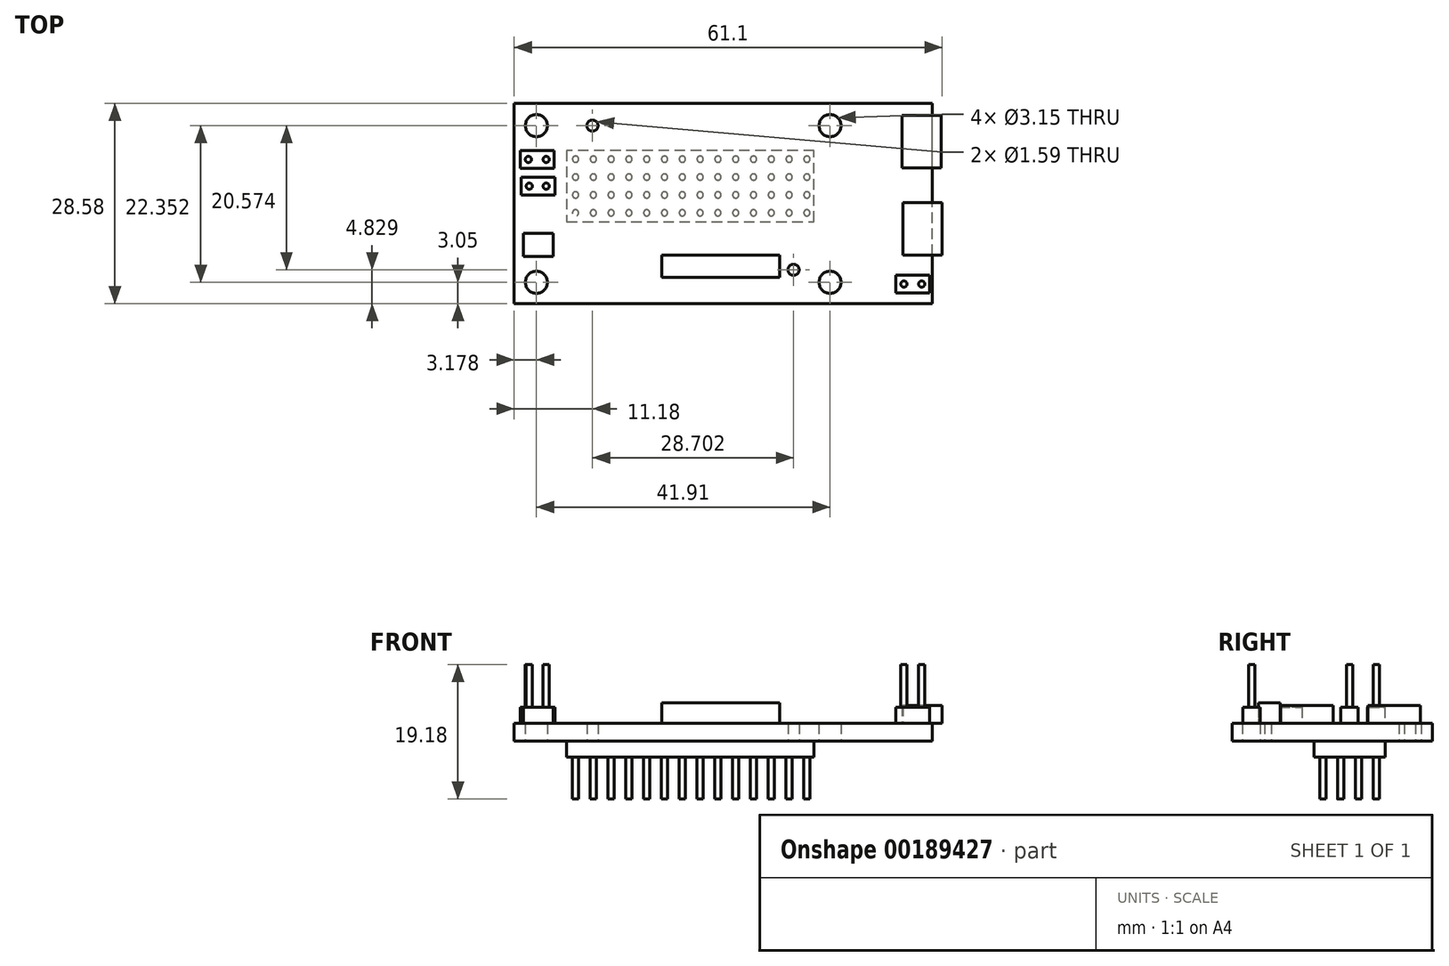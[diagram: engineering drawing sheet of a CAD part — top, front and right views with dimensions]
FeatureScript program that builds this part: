
annotation { "Feature Type Name" : "Feature", "Feature Type Description" : "" }
export const myFeature = defineFeature(function(context is Context, id is Id, definition is map)
    precondition{}
    {
        {
            var Q0;
            Q0=qCreatedBy(makeId("Top.planeOp"),FACE);
            var sketch = newSketch(context, id + "F0", { "sketchPlane" : qUnion([Q0])});
            skLineSegment(sketch, "E0", {"start": v(-22.44, -2) * mm, "end": v(-22.44, -0.67) * mm});
            skLineSegment(sketch, "E1", {"start": v(-22.44, -0.67) * mm, "end": v(-21.12, -0.67) * mm});
            skLineSegment(sketch, "E2", {"start": v(-21.12, -0.67) * mm, "end": v(-21.12, -2) * mm});
            skLineSegment(sketch, "E3", {"start": v(-21.12, -2) * mm, "end": v(-22.44, -2) * mm});
            skLineSegment(sketch, "E4", {"start": v(-22.44, 0.55) * mm, "end": v(-22.44, 1.87) * mm});
            skLineSegment(sketch, "E5", {"start": v(-22.44, 1.87) * mm, "end": v(-21.12, 1.87) * mm});
            skLineSegment(sketch, "E6", {"start": v(-21.12, 1.87) * mm, "end": v(-21.12, 0.55) * mm});
            skLineSegment(sketch, "E7", {"start": v(-21.12, 0.55) * mm, "end": v(-22.44, 0.55) * mm});
            skLineSegment(sketch, "E8", {"start": v(-22.44, 3.09) * mm, "end": v(-22.44, 4.4) * mm});
            skLineSegment(sketch, "E9", {"start": v(-22.44, 4.4) * mm, "end": v(-21.12, 4.4) * mm});
            skLineSegment(sketch, "E10", {"start": v(-21.12, 4.4) * mm, "end": v(-21.12, 3.09) * mm});
            skLineSegment(sketch, "E11", {"start": v(-21.12, 3.09) * mm, "end": v(-22.44, 3.09) * mm});
            skLineSegment(sketch, "E12", {"start": v(-22.44, 5.63) * mm, "end": v(-22.44, 6.95) * mm});
            skLineSegment(sketch, "E13", {"start": v(-22.44, 6.95) * mm, "end": v(-21.12, 6.95) * mm});
            skLineSegment(sketch, "E14", {"start": v(-21.12, 6.95) * mm, "end": v(-21.12, 5.63) * mm});
            skLineSegment(sketch, "E15", {"start": v(-21.12, 5.63) * mm, "end": v(-22.44, 5.63) * mm});
            skLineSegment(sketch, "E16", {"start": v(26.9, -10.78) * mm, "end": v(28.33, -10.78) * mm});
            skLineSegment(sketch, "E17", {"start": v(28.33, -10.78) * mm, "end": v(28.33, -12.2) * mm});
            skLineSegment(sketch, "E18", {"start": v(28.33, -12.2) * mm, "end": v(26.9, -12.2) * mm});
            skLineSegment(sketch, "E19", {"start": v(26.9, -12.2) * mm, "end": v(26.9, -10.78) * mm});
            skLineSegment(sketch, "E20", {"start": v(-27.68, 1.77) * mm, "end": v(-29.1, 1.77) * mm});
            skLineSegment(sketch, "E21", {"start": v(-29.1, 1.77) * mm, "end": v(-29.1, 3.19) * mm});
            skLineSegment(sketch, "E22", {"start": v(-29.1, 3.19) * mm, "end": v(-27.68, 3.19) * mm});
            skLineSegment(sketch, "E23", {"start": v(-27.68, 3.19) * mm, "end": v(-27.68, 1.77) * mm});
            skLineSegment(sketch, "E24", {"start": v(-27.8, 5.58) * mm, "end": v(-29.23, 5.58) * mm});
            skLineSegment(sketch, "E25", {"start": v(-29.23, 5.58) * mm, "end": v(-29.23, 7) * mm});
            skLineSegment(sketch, "E26", {"start": v(-29.23, 7) * mm, "end": v(-27.8, 7) * mm});
            skLineSegment(sketch, "E27", {"start": v(-27.8, 7) * mm, "end": v(-27.8, 5.58) * mm});
            skLineSegment(sketch, "E28", {"start": v(24.95, -7.37) * mm, "end": v(30.55, -7.37) * mm});
            skLineSegment(sketch, "E29", {"start": v(30.55, -7.37) * mm, "end": v(30.55, 0.13) * mm});
            skLineSegment(sketch, "E30", {"start": v(30.55, 0.13) * mm, "end": v(24.95, 0.13) * mm});
            skLineSegment(sketch, "E31", {"start": v(24.95, 0.13) * mm, "end": v(24.95, -7.37) * mm});
            skLineSegment(sketch, "E32", {"start": v(-29.24, -4.28) * mm, "end": v(-25, -4.28) * mm});
            skLineSegment(sketch, "E33", {"start": v(-25, -4.28) * mm, "end": v(-25, -7.53) * mm});
            skLineSegment(sketch, "E34", {"start": v(-25, -7.53) * mm, "end": v(-29.24, -7.53) * mm});
            skLineSegment(sketch, "E35", {"start": v(-29.24, -7.53) * mm, "end": v(-29.24, -4.28) * mm});
            skLineSegment(sketch, "E36", {"start": v(-23.05, -0.06) * mm, "end": v(-23.05, -2.6) * mm});
            skLineSegment(sketch, "E37", {"start": v(-23.05, -2.6) * mm, "end": v(2.35, -2.6) * mm});
            skLineSegment(sketch, "E38", {"start": v(2.35, -0.06) * mm, "end": v(-23.05, -0.06) * mm});
            skLineSegment(sketch, "E39", {"start": v(-23.05, 2.48) * mm, "end": v(-23.05, -0.06) * mm});
            skLineSegment(sketch, "E40", {"start": v(-23.05, -0.06) * mm, "end": v(2.35, -0.06) * mm});
            skLineSegment(sketch, "E41", {"start": v(2.35, 2.48) * mm, "end": v(-23.05, 2.48) * mm});
            skLineSegment(sketch, "E42", {"start": v(-23.05, 5.02) * mm, "end": v(-23.05, 2.48) * mm});
            skLineSegment(sketch, "E43", {"start": v(-23.05, 2.48) * mm, "end": v(2.35, 2.48) * mm});
            skLineSegment(sketch, "E44", {"start": v(2.35, 5.02) * mm, "end": v(-23.05, 5.02) * mm});
            skLineSegment(sketch, "E45", {"start": v(-23.05, 7.56) * mm, "end": v(-23.05, 5.02) * mm});
            skLineSegment(sketch, "E46", {"start": v(-23.05, 5.02) * mm, "end": v(2.35, 5.02) * mm});
            skLineSegment(sketch, "E47", {"start": v(2.35, 7.56) * mm, "end": v(-23.05, 7.56) * mm});
            skLineSegment(sketch, "E48", {"start": v(-9.46, -7.4) * mm, "end": v(7.34, -7.4) * mm});
            skLineSegment(sketch, "E49", {"start": v(7.34, -7.4) * mm, "end": v(7.34, -10.53) * mm});
            skLineSegment(sketch, "E50", {"start": v(7.34, -10.53) * mm, "end": v(-9.46, -10.53) * mm});
            skLineSegment(sketch, "E51", {"start": v(-9.46, -10.53) * mm, "end": v(-9.46, -7.4) * mm});
            skLineSegment(sketch, "E52", {"start": v(24.82, 5.08) * mm, "end": v(30.42, 5.08) * mm});
            skLineSegment(sketch, "E53", {"start": v(30.42, 5.08) * mm, "end": v(30.42, 12.58) * mm});
            skLineSegment(sketch, "E54", {"start": v(30.42, 12.58) * mm, "end": v(24.82, 12.58) * mm});
            skLineSegment(sketch, "E55", {"start": v(24.82, 12.58) * mm, "end": v(24.82, 5.08) * mm});
            skLineSegment(sketch, "E56", {"start": v(28.76, -10.25) * mm, "end": v(28.76, -12.74) * mm});
            skLineSegment(sketch, "E57", {"start": v(28.76, -12.74) * mm, "end": v(23.94, -12.74) * mm});
            skLineSegment(sketch, "E58", {"start": v(23.94, -12.74) * mm, "end": v(23.94, -10.25) * mm});
            skLineSegment(sketch, "E59", {"start": v(23.94, -10.25) * mm, "end": v(28.76, -10.25) * mm});
            skLineSegment(sketch, "E60", {"start": v(-29.53, 1.23) * mm, "end": v(-29.53, 3.72) * mm});
            skLineSegment(sketch, "E61", {"start": v(-29.53, 3.72) * mm, "end": v(-24.7, 3.72) * mm});
            skLineSegment(sketch, "E62", {"start": v(-24.7, 3.72) * mm, "end": v(-24.7, 1.23) * mm});
            skLineSegment(sketch, "E63", {"start": v(-24.7, 1.23) * mm, "end": v(-29.53, 1.23) * mm});
            skLineSegment(sketch, "E64", {"start": v(-29.66, 5.04) * mm, "end": v(-29.66, 7.53) * mm});
            skLineSegment(sketch, "E65", {"start": v(-29.66, 7.53) * mm, "end": v(-24.83, 7.53) * mm});
            skLineSegment(sketch, "E66", {"start": v(-24.83, 7.53) * mm, "end": v(-24.83, 5.04) * mm});
            skLineSegment(sketch, "E67", {"start": v(-24.83, 5.04) * mm, "end": v(-29.66, 5.04) * mm});
            skLineSegment(sketch, "E68", {"start": v(12.25, 5.02) * mm, "end": v(-13.15, 5.02) * mm});
            skLineSegment(sketch, "E69", {"start": v(-13.15, 5.02) * mm, "end": v(12.25, 5.02) * mm});
            skLineSegment(sketch, "E70", {"start": v(12.25, 5.02) * mm, "end": v(12.25, 7.56) * mm});
            skLineSegment(sketch, "E71", {"start": v(12.25, 7.56) * mm, "end": v(-13.15, 7.56) * mm});
            skLineSegment(sketch, "E72", {"start": v(12.25, -0.06) * mm, "end": v(-13.15, -0.06) * mm});
            skLineSegment(sketch, "E73", {"start": v(-13.15, -0.06) * mm, "end": v(12.25, -0.06) * mm});
            skLineSegment(sketch, "E74", {"start": v(12.25, -0.06) * mm, "end": v(12.25, 2.48) * mm});
            skLineSegment(sketch, "E75", {"start": v(12.25, 2.48) * mm, "end": v(-13.15, 2.48) * mm});
            skLineSegment(sketch, "E76", {"start": v(-13.15, 2.48) * mm, "end": v(12.25, 2.48) * mm});
            skLineSegment(sketch, "E77", {"start": v(12.25, 2.48) * mm, "end": v(12.25, 5.02) * mm});
            skLineSegment(sketch, "E78", {"start": v(-13.15, -2.6) * mm, "end": v(12.25, -2.6) * mm});
            skLineSegment(sketch, "E79", {"start": v(12.25, -2.6) * mm, "end": v(12.25, -0.06) * mm});
            skLineSegment(sketch, "E80", {"start": v(-30.55, 14.29) * mm, "end": v(-30.55, -14.29) * mm});
            skLineSegment(sketch, "E81", {"start": v(-30.55, -14.29) * mm, "end": v(29.14, -14.29) * mm});
            skLineSegment(sketch, "E82", {"start": v(29.14, -14.29) * mm, "end": v(29.14, 14.29) * mm});
            skLineSegment(sketch, "E83", {"start": v(29.14, 14.29) * mm, "end": v(-30.55, 14.29) * mm});
            skSolve(sketch);
        }
        {
            var Q0;
            Q0=qCreatedBy(makeId("Top.planeOp"),FACE);
            var sketch = newSketch(context, id + "F1", { "sketchPlane" : qUnion([Q0])});
            skLineSegment(sketch, "E84.0", {"start": v(-30.55, 14.29) * mm, "end": v(-30.55, -14.29) * mm});
            skLineSegment(sketch, "E84.1", {"start": v(-30.55, -14.29) * mm, "end": v(29.14, -14.29) * mm});
            skLineSegment(sketch, "E84.2", {"start": v(29.14, 14.29) * mm, "end": v(-30.55, 14.29) * mm});
            skLineSegment(sketch, "E84.3", {"start": v(29.14, -14.29) * mm, "end": v(29.14, 14.29) * mm});
            skCircle(sketch, "E85", {"center": v(-27.37, 11.11) * mm, "radius": 1.57 * mm});
            skCircle(sketch, "E86", {"center": v(14.54, 11.11) * mm, "radius": 1.57 * mm});
            skCircle(sketch, "E87", {"center": v(14.54, -11.24) * mm, "radius": 1.57 * mm});
            skCircle(sketch, "E88", {"center": v(-27.37, -11.24) * mm, "radius": 1.57 * mm});
            skCircle(sketch, "E89", {"center": v(-19.37, 11.11) * mm, "radius": 0.8 * mm});
            skCircle(sketch, "E90", {"center": v(9.33, -9.46) * mm, "radius": 0.8 * mm});
            skSolve(sketch);
        }
        {
            var Q0;
            Q0 = qSketchRegion(id + "F1", true);
            extrude(context, id + "F2", {"entities" : qUnion([Q0]), "depth" : 2.54 * mm});
        }
        {
            var Q0;
            Q0=makeQuery(id+"F2.opExtrude","CAP_FACE",FACE,{"disambiguationData":[OSD([sQuery(id+"F1.wireOp",EDGE,"E84.0"),sQuery(id+"F1.wireOp",EDGE,"E84.1"),sQuery(id+"F1.wireOp",EDGE,"E84.2"),sQuery(id+"F1.wireOp",EDGE,"E84.3"),sQuery(id+"F1.wireOp",EDGE,"E85"),sQuery(id+"F1.wireOp",EDGE,"E86"),sQuery(id+"F1.wireOp",EDGE,"E87"),sQuery(id+"F1.wireOp",EDGE,"E88"),sQuery(id+"F1.wireOp",EDGE,"E89"),sQuery(id+"F1.wireOp",EDGE,"E90")])],"isStart":false});
            var sketch = newSketch(context, id + "F3", { "sketchPlane" : qUnion([Q0])});
            skLineSegment(sketch, "E91.0", {"start": v(30.42, 12.58) * mm, "end": v(24.82, 12.58) * mm});
            skLineSegment(sketch, "E91.1", {"start": v(30.42, 5.08) * mm, "end": v(30.42, 12.58) * mm});
            skLineSegment(sketch, "E91.2", {"start": v(24.82, 5.08) * mm, "end": v(30.42, 5.08) * mm});
            skLineSegment(sketch, "E91.3", {"start": v(24.82, 12.58) * mm, "end": v(24.82, 5.08) * mm});
            skLineSegment(sketch, "E91.4", {"start": v(30.55, 0.13) * mm, "end": v(24.95, 0.13) * mm});
            skLineSegment(sketch, "E91.5", {"start": v(30.55, -7.37) * mm, "end": v(30.55, 0.13) * mm});
            skLineSegment(sketch, "E91.6", {"start": v(24.95, -7.37) * mm, "end": v(30.55, -7.37) * mm});
            skLineSegment(sketch, "E91.7", {"start": v(24.95, 0.13) * mm, "end": v(24.95, -7.37) * mm});
            skSolve(sketch);
        }
        {
            var Q0;
            Q0 = qSketchRegion(id + "F3", true);
            extrude(context, id + "F4", {"entities" : qUnion([Q0]), "operationType" : NewBodyOperationType.ADD, "depth" : 2.54 * mm});
        }
        {
            var Q0;
            Q0=makeQuery(id+"F2.opExtrude","CAP_FACE",FACE,{"disambiguationData":[OSD([sQuery(id+"F1.wireOp",EDGE,"E84.0"),sQuery(id+"F1.wireOp",EDGE,"E84.1"),sQuery(id+"F1.wireOp",EDGE,"E84.2"),sQuery(id+"F1.wireOp",EDGE,"E84.3"),sQuery(id+"F1.wireOp",EDGE,"E85"),sQuery(id+"F1.wireOp",EDGE,"E86"),sQuery(id+"F1.wireOp",EDGE,"E87"),sQuery(id+"F1.wireOp",EDGE,"E88"),sQuery(id+"F1.wireOp",EDGE,"E89"),sQuery(id+"F1.wireOp",EDGE,"E90")])],"isStart":false});
            var sketch = newSketch(context, id + "F5", { "sketchPlane" : qUnion([Q0])});
            skLineSegment(sketch, "E92.0", {"start": v(-9.46, -7.4) * mm, "end": v(7.34, -7.4) * mm});
            skLineSegment(sketch, "E92.1", {"start": v(7.34, -7.4) * mm, "end": v(7.34, -10.53) * mm});
            skLineSegment(sketch, "E92.2", {"start": v(7.34, -10.53) * mm, "end": v(-9.46, -10.53) * mm});
            skLineSegment(sketch, "E92.3", {"start": v(-9.46, -10.53) * mm, "end": v(-9.46, -7.4) * mm});
            skSolve(sketch);
        }
        {
            var Q0;
            Q0 = qSketchRegion(id + "F5", true);
            extrude(context, id + "F6", {"entities" : qUnion([Q0]), "operationType" : NewBodyOperationType.ADD, "depth" : 2.92 * mm});
        }
        {
            var Q0;
            Q0=makeQuery(id+"F2.opExtrude","CAP_FACE",FACE,{"disambiguationData":[OSD([sQuery(id+"F1.wireOp",EDGE,"E84.0"),sQuery(id+"F1.wireOp",EDGE,"E84.1"),sQuery(id+"F1.wireOp",EDGE,"E84.2"),sQuery(id+"F1.wireOp",EDGE,"E84.3"),sQuery(id+"F1.wireOp",EDGE,"E85"),sQuery(id+"F1.wireOp",EDGE,"E86"),sQuery(id+"F1.wireOp",EDGE,"E87"),sQuery(id+"F1.wireOp",EDGE,"E88"),sQuery(id+"F1.wireOp",EDGE,"E89"),sQuery(id+"F1.wireOp",EDGE,"E90")])],"isStart":false});
            var sketch = newSketch(context, id + "F7", { "sketchPlane" : qUnion([Q0])});
            skLineSegment(sketch, "E93.0", {"start": v(23.94, -10.25) * mm, "end": v(28.76, -10.25) * mm});
            skLineSegment(sketch, "E93.1", {"start": v(23.94, -12.74) * mm, "end": v(23.94, -10.25) * mm});
            skLineSegment(sketch, "E93.2", {"start": v(28.76, -12.74) * mm, "end": v(23.94, -12.74) * mm});
            skLineSegment(sketch, "E93.3", {"start": v(28.76, -10.25) * mm, "end": v(28.76, -12.74) * mm});
            skLineSegment(sketch, "E93.4", {"start": v(-24.83, 5.04) * mm, "end": v(-29.66, 5.04) * mm});
            skLineSegment(sketch, "E93.5", {"start": v(-24.83, 7.53) * mm, "end": v(-24.83, 5.04) * mm});
            skLineSegment(sketch, "E93.6", {"start": v(-29.66, 7.53) * mm, "end": v(-24.83, 7.53) * mm});
            skLineSegment(sketch, "E93.7", {"start": v(-29.66, 5.04) * mm, "end": v(-29.66, 7.53) * mm});
            skLineSegment(sketch, "E93.8", {"start": v(-29.53, 1.23) * mm, "end": v(-29.53, 3.72) * mm});
            skLineSegment(sketch, "E93.9", {"start": v(-29.53, 3.72) * mm, "end": v(-24.7, 3.72) * mm});
            skLineSegment(sketch, "E93.10", {"start": v(-24.7, 3.72) * mm, "end": v(-24.7, 1.23) * mm});
            skLineSegment(sketch, "E93.11", {"start": v(-24.7, 1.23) * mm, "end": v(-29.53, 1.23) * mm});
            skLineSegment(sketch, "E93.12", {"start": v(-29.24, -4.28) * mm, "end": v(-25, -4.28) * mm});
            skLineSegment(sketch, "E93.13", {"start": v(-25, -4.28) * mm, "end": v(-25, -7.53) * mm});
            skLineSegment(sketch, "E93.14", {"start": v(-25, -7.53) * mm, "end": v(-29.24, -7.53) * mm});
            skLineSegment(sketch, "E93.15", {"start": v(-29.24, -7.53) * mm, "end": v(-29.24, -4.28) * mm});
            skSolve(sketch);
        }
        {
            var Q0;
            Q0 = qSketchRegion(id + "F7", true);
            extrude(context, id + "F8", {"entities" : qUnion([Q0]), "operationType" : NewBodyOperationType.ADD, "depth" : 2.3 * mm});
        }
        {
            var Q0;
            Q0=makeQuery(id+"F8.opExtrude","CAP_FACE",FACE,{"disambiguationData":[OSD([sQuery(id+"F7.wireOp",EDGE,"E93.4"),sQuery(id+"F7.wireOp",EDGE,"E93.5"),sQuery(id+"F7.wireOp",EDGE,"E93.6"),sQuery(id+"F7.wireOp",EDGE,"E93.7")])],"isStart":false});
            var sketch = newSketch(context, id + "F9", { "sketchPlane" : qUnion([Q0])});
            skCircle(sketch, "E94", {"center": v(-28.51, 6.29) * mm, "radius": 0.44 * mm});
            skCircle(sketch, "E95", {"center": v(-25.97, 6.29) * mm, "radius": 0.44 * mm});
            skCircle(sketch, "E96", {"center": v(-28.39, 2.48) * mm, "radius": 0.44 * mm});
            skCircle(sketch, "E97", {"center": v(-25.97, 2.48) * mm, "radius": 0.44 * mm});
            skCircle(sketch, "E98", {"center": v(27.62, -11.5) * mm, "radius": 0.44 * mm});
            skCircle(sketch, "E99", {"center": v(25.08, -11.5) * mm, "radius": 0.44 * mm});
            skPoint(sketch, "E100.0", {"position": v(28.33, -10.78) * mm});
            skPoint(sketch, "E100.1", {"position": v(26.9, -12.2) * mm});
            skLineSegment(sketch, "E101", {"start": v(28.33, -10.78) * mm, "end": v(26.9, -12.2) * mm, "construction": true});
            skPoint(sketch, "E102.0", {"position": v(-27.8, 7) * mm});
            skPoint(sketch, "E102.1", {"position": v(-29.23, 5.58) * mm});
            skPoint(sketch, "E102.2", {"position": v(-29.1, 3.19) * mm});
            skPoint(sketch, "E102.3", {"position": v(-27.68, 1.77) * mm});
            skLineSegment(sketch, "E103", {"start": v(-27.8, 7) * mm, "end": v(-29.23, 5.58) * mm, "construction": true});
            skLineSegment(sketch, "E104", {"start": v(-29.1, 3.19) * mm, "end": v(-27.68, 1.77) * mm, "construction": true});
            skSolve(sketch);
        }
        {
            var Q0;
            Q0 = qSketchRegion(id + "F9", true);
            extrude(context, id + "F10", {"entities" : qUnion([Q0]), "operationType" : NewBodyOperationType.ADD, "depth" : 6.1 * mm});
        }
        {
            var Q0;
            {var subQ9=sQuery(id+"F0.wireOp",EDGE,"E31");Q0=makeQuery(id+"F0.imprint","IMPRINT",FACE,{"disambiguationData":[TD([[makeQuery(id+"F0.imprint","IMPRINT",EDGE,{"derivedFrom":subQ9}),-1.0]])]});}
            var sketch = newSketch(context, id + "F11", { "sketchPlane" : qUnion([Q0])});
            skLineSegment(sketch, "E105.bottom", {"start": v(-23.05, -2.6) * mm, "end": v(12.25, -2.6) * mm});
            skLineSegment(sketch, "E105.top", {"start": v(-23.05, 7.56) * mm, "end": v(12.25, 7.56) * mm});
            skLineSegment(sketch, "E105.left", {"start": v(-23.05, -2.6) * mm, "end": v(-23.05, 7.56) * mm});
            skLineSegment(sketch, "E105.right", {"start": v(12.25, -2.6) * mm, "end": v(12.25, 7.56) * mm});
            skSolve(sketch);
        }
        {
            var Q0;
            Q0 = qSketchRegion(id + "F11", true);
            extrude(context, id + "F12", {"entities" : qUnion([Q0]), "operationType" : NewBodyOperationType.ADD, "oppositeDirection" : true, "depth" : 2.3 * mm});
        }
        {
            var Q0;
            Q0=makeQuery(id+"F12.opExtrude","CAP_FACE",FACE,{"disambiguationData":[OSD([sQuery(id+"F11.wireOp",EDGE,"E105.bottom"),sQuery(id+"F11.wireOp",EDGE,"E105.top"),sQuery(id+"F11.wireOp",EDGE,"E105.left"),sQuery(id+"F11.wireOp",EDGE,"E105.right")])],"isStart":false});
            var sketch = newSketch(context, id + "F13", { "sketchPlane" : qUnion([Q0])});
            skLineSegment(sketch, "E106", {"start": v(-22.44, 2) * mm, "end": v(-21.12, 0.67) * mm, "construction": true});
            skCircle(sketch, "E107", {"center": v(-21.78, 1.33) * mm, "radius": 0.44 * mm});
            skCircle(sketch, "E108.1.0.0", {"center": v(-19.24, 1.33) * mm, "radius": 0.44 * mm});
            skCircle(sketch, "E108.2.0.0", {"center": v(-16.7, 1.33) * mm, "radius": 0.44 * mm});
            skCircle(sketch, "E108.3.0.0", {"center": v(-14.16, 1.33) * mm, "radius": 0.44 * mm});
            skCircle(sketch, "E108.4.0.0", {"center": v(-11.62, 1.33) * mm, "radius": 0.44 * mm});
            skCircle(sketch, "E108.5.0.0", {"center": v(-9.08, 1.33) * mm, "radius": 0.44 * mm});
            skCircle(sketch, "E108.6.0.0", {"center": v(-6.54, 1.33) * mm, "radius": 0.44 * mm});
            skCircle(sketch, "E108.7.0.0", {"center": v(-4, 1.33) * mm, "radius": 0.44 * mm});
            skCircle(sketch, "E108.8.0.0", {"center": v(-1.46, 1.33) * mm, "radius": 0.44 * mm});
            skCircle(sketch, "E108.9.0.0", {"center": v(1.08, 1.33) * mm, "radius": 0.44 * mm});
            skCircle(sketch, "E108.10.0.0", {"center": v(3.62, 1.33) * mm, "radius": 0.44 * mm});
            skCircle(sketch, "E108.11.0.0", {"center": v(6.16, 1.33) * mm, "radius": 0.44 * mm});
            skCircle(sketch, "E108.12.0.0", {"center": v(8.7, 1.33) * mm, "radius": 0.44 * mm});
            skCircle(sketch, "E108.13.0.0", {"center": v(11.24, 1.33) * mm, "radius": 0.44 * mm});
            skLineSegment(sketch, "E108.direction1", {"start": v(-21.78, 1.33) * mm, "end": v(-19.24, 1.33) * mm, "construction": true});
            skCircle(sketch, "E109.1.0.0", {"center": v(-21.78, -1.22) * mm, "radius": 0.44 * mm});
            skCircle(sketch, "E109.1.0.1", {"center": v(-19.24, -1.22) * mm, "radius": 0.44 * mm});
            skCircle(sketch, "E109.1.0.2", {"center": v(-16.7, -1.22) * mm, "radius": 0.44 * mm});
            skCircle(sketch, "E109.1.0.3", {"center": v(-14.16, -1.22) * mm, "radius": 0.44 * mm});
            skCircle(sketch, "E109.1.0.4", {"center": v(-11.62, -1.22) * mm, "radius": 0.44 * mm});
            skCircle(sketch, "E109.1.0.5", {"center": v(-9.08, -1.22) * mm, "radius": 0.44 * mm});
            skCircle(sketch, "E109.1.0.6", {"center": v(-6.54, -1.22) * mm, "radius": 0.44 * mm});
            skCircle(sketch, "E109.1.0.7", {"center": v(-4, -1.22) * mm, "radius": 0.44 * mm});
            skCircle(sketch, "E109.1.0.8", {"center": v(-1.46, -1.22) * mm, "radius": 0.44 * mm});
            skCircle(sketch, "E109.1.0.9", {"center": v(1.08, -1.22) * mm, "radius": 0.44 * mm});
            skCircle(sketch, "E109.1.0.10", {"center": v(3.62, -1.22) * mm, "radius": 0.44 * mm});
            skCircle(sketch, "E109.1.0.11", {"center": v(6.16, -1.22) * mm, "radius": 0.44 * mm});
            skCircle(sketch, "E109.1.0.12", {"center": v(8.7, -1.22) * mm, "radius": 0.44 * mm});
            skCircle(sketch, "E109.1.0.13", {"center": v(11.24, -1.22) * mm, "radius": 0.44 * mm});
            skCircle(sketch, "E109.2.0.0", {"center": v(-21.78, -3.77) * mm, "radius": 0.44 * mm});
            skCircle(sketch, "E109.2.0.1", {"center": v(-19.24, -3.77) * mm, "radius": 0.44 * mm});
            skCircle(sketch, "E109.2.0.2", {"center": v(-16.7, -3.77) * mm, "radius": 0.44 * mm});
            skCircle(sketch, "E109.2.0.3", {"center": v(-14.16, -3.77) * mm, "radius": 0.44 * mm});
            skCircle(sketch, "E109.2.0.4", {"center": v(-11.62, -3.77) * mm, "radius": 0.44 * mm});
            skCircle(sketch, "E109.2.0.5", {"center": v(-9.08, -3.77) * mm, "radius": 0.44 * mm});
            skCircle(sketch, "E109.2.0.6", {"center": v(-6.54, -3.77) * mm, "radius": 0.44 * mm});
            skCircle(sketch, "E109.2.0.7", {"center": v(-4, -3.77) * mm, "radius": 0.44 * mm});
            skCircle(sketch, "E109.2.0.8", {"center": v(-1.46, -3.77) * mm, "radius": 0.44 * mm});
            skCircle(sketch, "E109.2.0.9", {"center": v(1.08, -3.77) * mm, "radius": 0.44 * mm});
            skCircle(sketch, "E109.2.0.10", {"center": v(3.62, -3.77) * mm, "radius": 0.44 * mm});
            skCircle(sketch, "E109.2.0.11", {"center": v(6.16, -3.77) * mm, "radius": 0.44 * mm});
            skCircle(sketch, "E109.2.0.12", {"center": v(8.7, -3.77) * mm, "radius": 0.44 * mm});
            skCircle(sketch, "E109.2.0.13", {"center": v(11.24, -3.77) * mm, "radius": 0.44 * mm});
            skCircle(sketch, "E109.3.0.0", {"center": v(-21.78, -6.32) * mm, "radius": 0.44 * mm});
            skCircle(sketch, "E109.3.0.1", {"center": v(-19.24, -6.32) * mm, "radius": 0.44 * mm});
            skCircle(sketch, "E109.3.0.2", {"center": v(-16.7, -6.32) * mm, "radius": 0.44 * mm});
            skCircle(sketch, "E109.3.0.3", {"center": v(-14.16, -6.32) * mm, "radius": 0.44 * mm});
            skCircle(sketch, "E109.3.0.4", {"center": v(-11.62, -6.32) * mm, "radius": 0.44 * mm});
            skCircle(sketch, "E109.3.0.5", {"center": v(-9.08, -6.32) * mm, "radius": 0.44 * mm});
            skCircle(sketch, "E109.3.0.6", {"center": v(-6.54, -6.32) * mm, "radius": 0.44 * mm});
            skCircle(sketch, "E109.3.0.7", {"center": v(-4, -6.32) * mm, "radius": 0.44 * mm});
            skCircle(sketch, "E109.3.0.8", {"center": v(-1.46, -6.32) * mm, "radius": 0.44 * mm});
            skCircle(sketch, "E109.3.0.9", {"center": v(1.08, -6.32) * mm, "radius": 0.44 * mm});
            skCircle(sketch, "E109.3.0.10", {"center": v(3.62, -6.32) * mm, "radius": 0.44 * mm});
            skCircle(sketch, "E109.3.0.11", {"center": v(6.16, -6.32) * mm, "radius": 0.44 * mm});
            skCircle(sketch, "E109.3.0.12", {"center": v(8.7, -6.32) * mm, "radius": 0.44 * mm});
            skCircle(sketch, "E109.3.0.13", {"center": v(11.24, -6.32) * mm, "radius": 0.44 * mm});
            skLineSegment(sketch, "E109.direction1", {"start": v(-21.78, 1.33) * mm, "end": v(-21.78, -1.22) * mm, "construction": true});
            skSolve(sketch);
        }
        {
            var Q0;
            Q0 = qSketchRegion(id + "F13", true);
            extrude(context, id + "F14", {"entities" : qUnion([Q0]), "operationType" : NewBodyOperationType.ADD, "depth" : 5.97 * mm});
        }
    });
